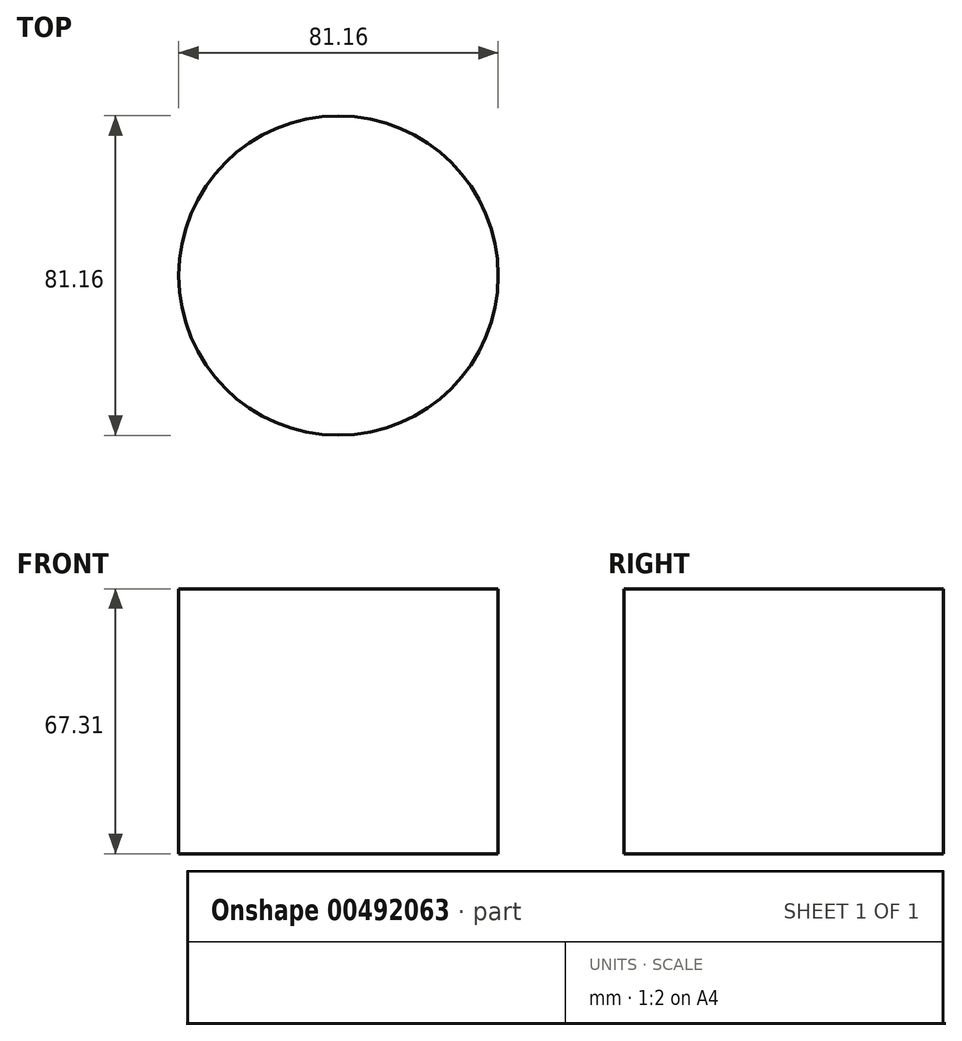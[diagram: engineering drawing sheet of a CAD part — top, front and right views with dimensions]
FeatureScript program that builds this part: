
annotation { "Feature Type Name" : "Feature", "Feature Type Description" : "" }
export const myFeature = defineFeature(function(context is Context, id is Id, definition is map)
    precondition{}
    {
        {
            var Q0;
            Q0=qCreatedBy(makeId("Top.planeOp"),FACE);
            var sketch = newSketch(context, id + "F0", { "sketchPlane" : qUnion([Q0])});
            skCircle(sketch, "E0", {"center": v(0, 0) * mm, "radius": 40.58 * mm});
            skSolve(sketch);
        }
        {
            var Q0;
            Q0=makeQuery(id+"F0.imprint","IMPRINT",FACE,{"disambiguationData":[TD([[makeQuery(id+"F0.imprint","IMPRINT",EDGE,{"derivedFrom":sQuery(id+"F0.wireOp",EDGE,"E0")}),1.0]])]});
            extrude(context, id + "F1", {"entities" : qUnion([Q0]), "depth" : 67.3 * mm});
        }
    });
